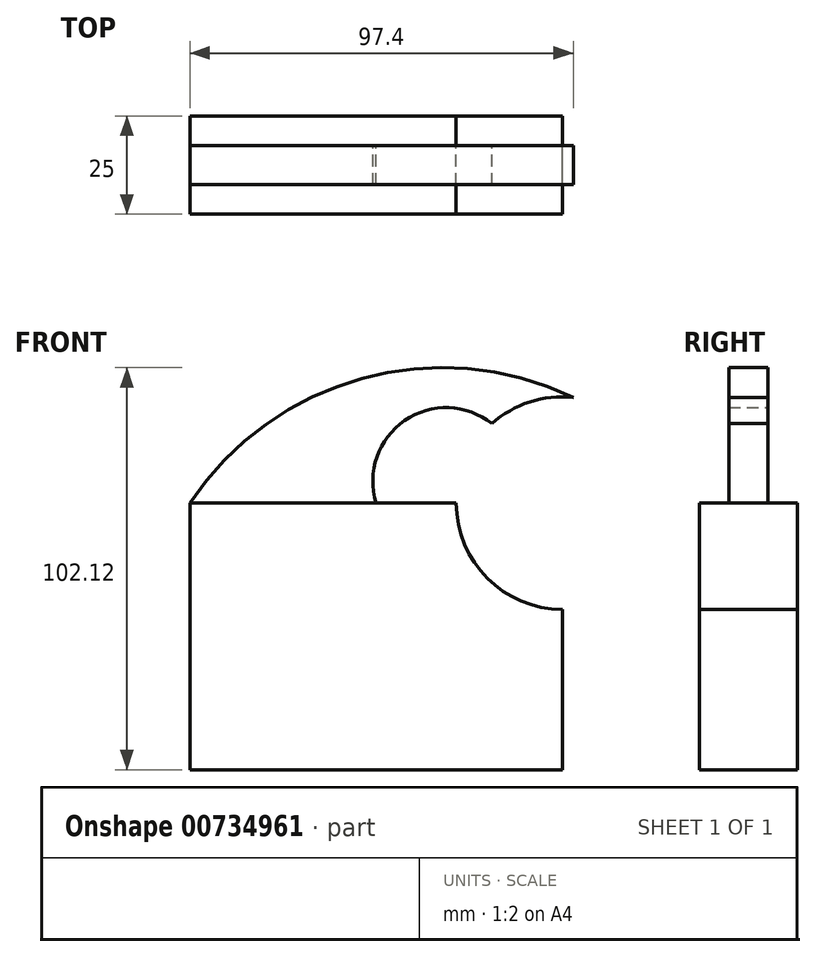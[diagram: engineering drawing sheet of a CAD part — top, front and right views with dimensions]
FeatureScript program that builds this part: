
annotation { "Feature Type Name" : "Feature", "Feature Type Description" : "" }
export const myFeature = defineFeature(function(context is Context, id is Id, definition is map)
    precondition{}
    {
        {
            var Q0;
            Q0=qCreatedBy(makeId("Front.planeOp"),FACE);
            var sketch = newSketch(context, id + "F0", { "sketchPlane" : qUnion([Q0])});
            skLineSegment(sketch, "E0.bottom", {"start": v(47.34, -33.87) * mm, "end": v(-47.34, -33.87) * mm});
            skLineSegment(sketch, "E0.top", {"start": v(47.34, 33.87) * mm, "end": v(-47.34, 33.87) * mm});
            skLineSegment(sketch, "E0.left", {"start": v(47.34, -33.87) * mm, "end": v(47.34, 33.87) * mm});
            skLineSegment(sketch, "E0.right", {"start": v(-47.34, -33.87) * mm, "end": v(-47.34, 33.87) * mm});
            skPoint(sketch, "E0.middle", {"position": v(0, 0) * mm});
            skCircle(sketch, "E1", {"center": v(47.34, 33.87) * mm, "radius": 27 * mm});
            skArc(sketch, "E2", {"start": v(50.06, 60.73) * mm, "mid": v(-3.65, 65.47) * mm, "end": v(-47.34, 33.87) * mm});
            skArc(sketch, "E3", {"start": v(29.4, 54.04) * mm, "mid": v(7.22, 54.84) * mm, "end": v(0, 33.87) * mm});
            skSolve(sketch);
        }
        {
            var Q0;
            {var subQ1=sQuery(id+"F0.wireOp",EDGE,"E0.bottom");Q0=makeQuery(id+"F0.imprint","IMPRINT",FACE,{"disambiguationData":[TD([[makeQuery(id+"F0.imprint","IMPRINT",EDGE,{"derivedFrom":subQ1}),-1.0]])]});}
            extrude(context, id + "F1", {"entities" : qUnion([Q0]), "endBound" : BoundingType.SYMMETRIC, "depth" : 25 * mm, "offsetDistance" : 25 * mm});
        }
        {
            var Q0;
            {var subQ0=sQuery(id+"F0.wireOp",EDGE,"E2");Q0=makeQuery(id+"F0.imprint","IMPRINT",FACE,{"disambiguationData":[TD([[makeQuery(id+"F0.imprint","IMPRINT",EDGE,{"derivedFrom":subQ0}),1.0]])]});}
            extrude(context, id + "F2", {"entities" : qUnion([Q0]), "operationType" : NewBodyOperationType.ADD, "endBound" : BoundingType.SYMMETRIC, "depth" : 10 * mm, "offsetDistance" : 25 * mm});
        }
    });
